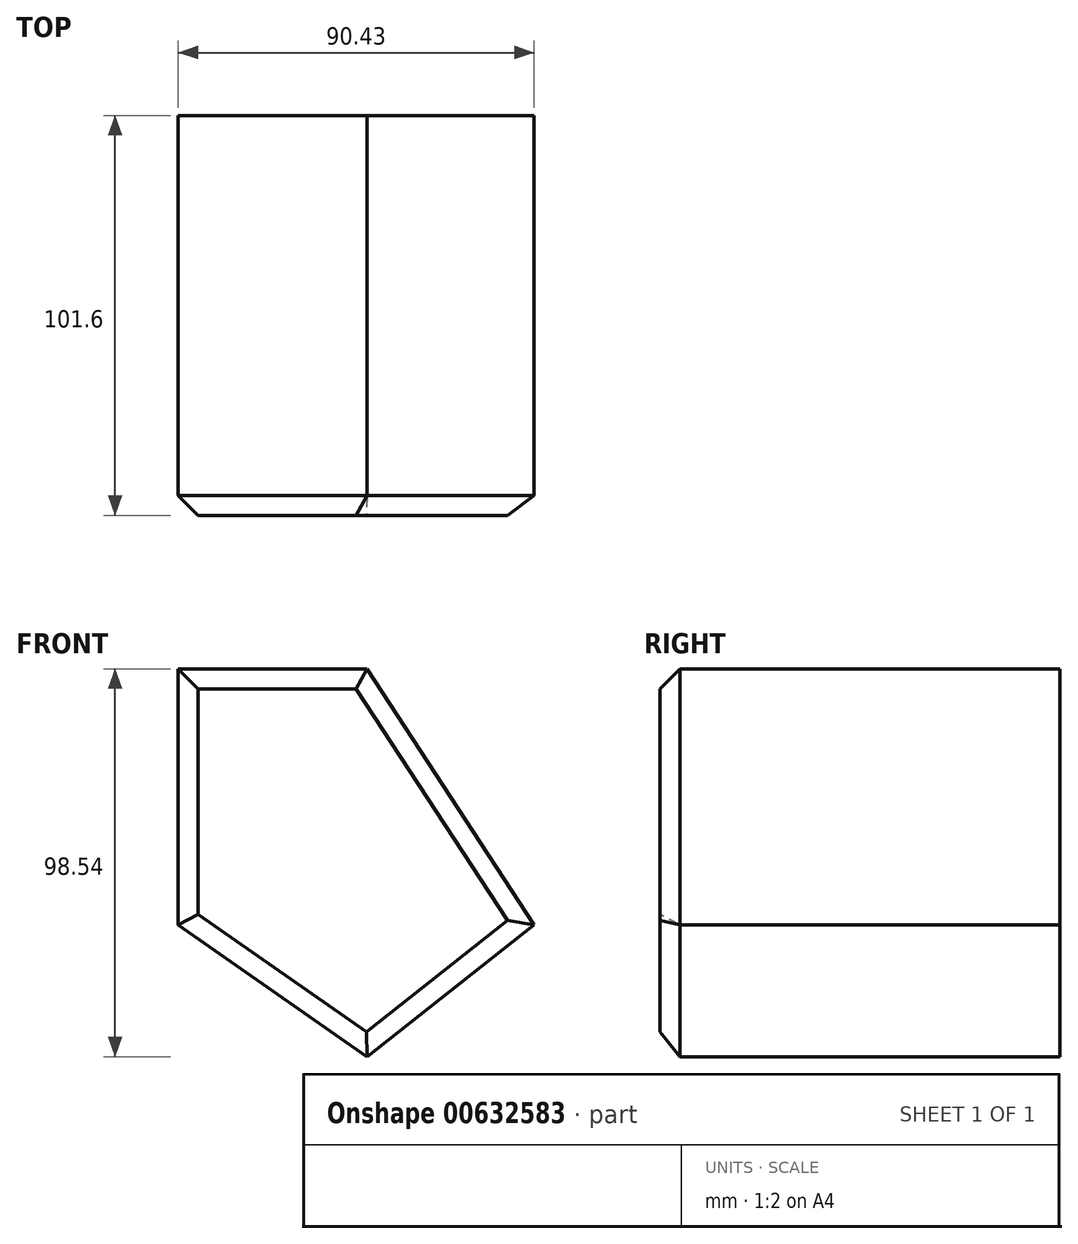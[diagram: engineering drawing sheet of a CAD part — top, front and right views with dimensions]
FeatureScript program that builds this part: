
annotation { "Feature Type Name" : "Feature", "Feature Type Description" : "" }
export const myFeature = defineFeature(function(context is Context, id is Id, definition is map)
    precondition{}
    {
        {
            var Q0;
            Q0=qCreatedBy(makeId("Front.planeOp"),FACE);
            var sketch = newSketch(context, id + "F0", { "sketchPlane" : qUnion([Q0])});
            skLineSegment(sketch, "E0", {"start": v(-48, 65.1) * mm, "end": v(0, 65.1) * mm});
            skLineSegment(sketch, "E1", {"start": v(0, 65.1) * mm, "end": v(42.44, 0) * mm});
            skLineSegment(sketch, "E2", {"start": v(42.44, 0) * mm, "end": v(0, -33.45) * mm});
            skLineSegment(sketch, "E3", {"start": v(0, -33.45) * mm, "end": v(-48, 0) * mm});
            skLineSegment(sketch, "E4", {"start": v(-48, 0) * mm, "end": v(-48, 65.1) * mm});
            skSolve(sketch);
        }
        {
            var Q0;
            Q0=makeQuery(id+"F0.imprint","IMPRINT",FACE,{"disambiguationData":[TD([[makeQuery(id+"F0.imprint","IMPRINT",EDGE,{"derivedFrom":sQuery(id+"F0.wireOp",EDGE,"E0")}),-1.0]])]});
            extrude(context, id + "F1", {"entities" : qUnion([Q0]), "depth" : 101.6 * mm, "offsetDistance" : 25.4 * mm});
        }
        {
            var Q0;
            Q0=makeQuery(id+"F1.opExtrude","CAP_FACE",FACE,{"disambiguationData":[OSD([sQuery(id+"F0.wireOp",EDGE,"E0"),sQuery(id+"F0.wireOp",EDGE,"E1"),sQuery(id+"F0.wireOp",EDGE,"E2"),sQuery(id+"F0.wireOp",EDGE,"E3"),sQuery(id+"F0.wireOp",EDGE,"E4")])],"isStart":false});
            chamfer(context, id + "F2", {"entities" : qUnion([Q0]), "width" : 5.08 * mm, "tangentPropagation" : true});
        }
    });
